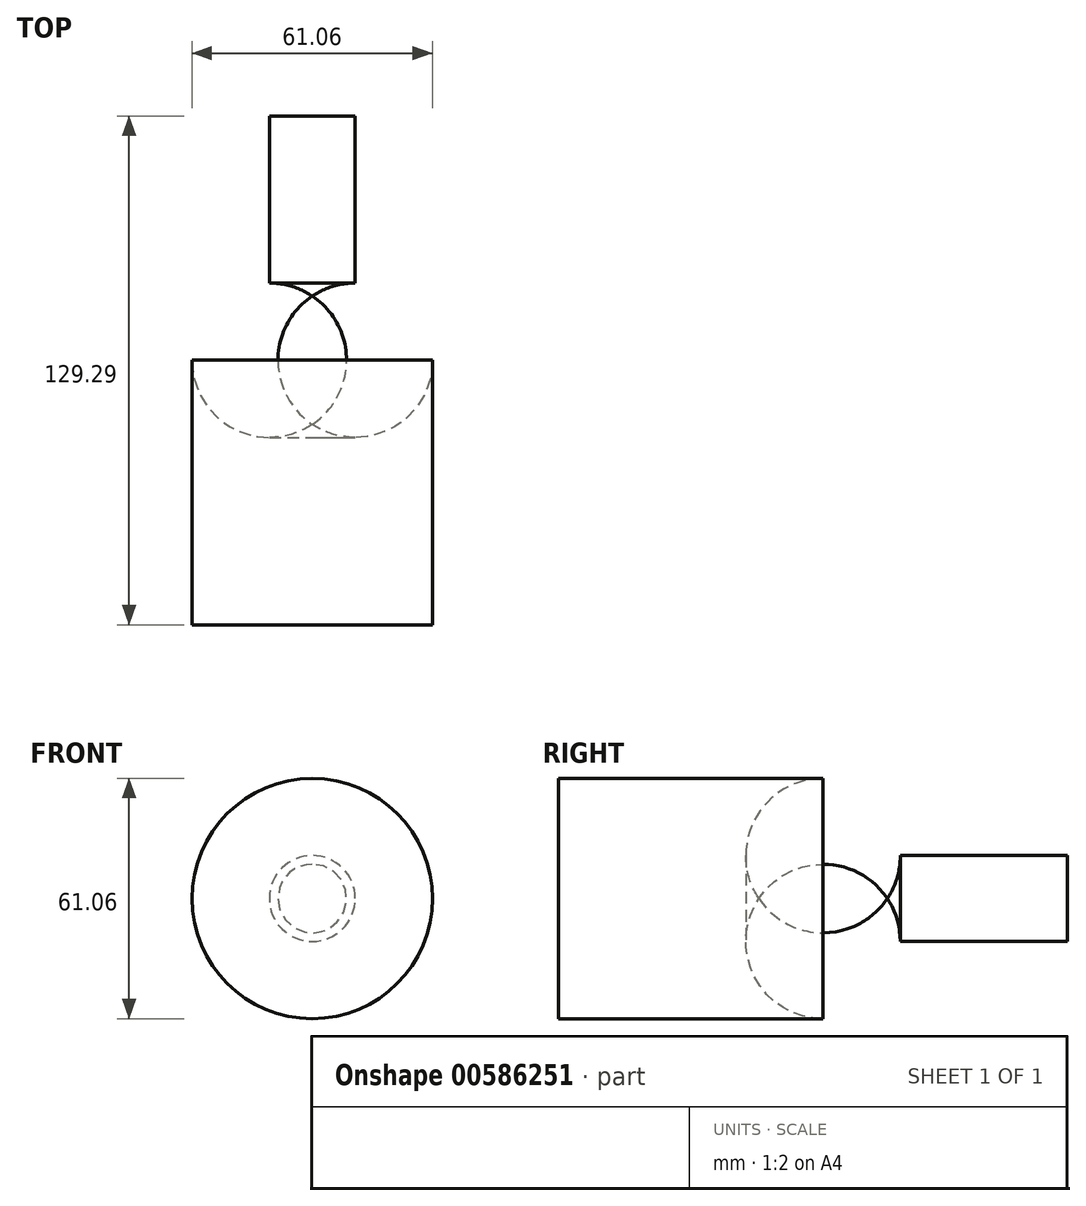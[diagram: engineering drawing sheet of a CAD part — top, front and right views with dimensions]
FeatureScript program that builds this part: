
annotation { "Feature Type Name" : "Feature", "Feature Type Description" : "" }
export const myFeature = defineFeature(function(context is Context, id is Id, definition is map)
    precondition{}
    {
        {
            var Q0;
            Q0=qCreatedBy(makeId("Front.planeOp"),FACE);
            var sketch = newSketch(context, id + "F0", { "sketchPlane" : qUnion([Q0])});
            skCircle(sketch, "E0", {"center": v(0, 0) * mm, "radius": 30.53 * mm});
            skSolve(sketch);
        }
        {
            var Q0;
            Q0=makeQuery(id+"F0.imprint","IMPRINT",FACE,{"disambiguationData":[TD([[makeQuery(id+"F0.imprint","IMPRINT",EDGE,{"derivedFrom":sQuery(id+"F0.wireOp",EDGE,"E0")}),1.0]])]});
            extrude(context, id + "F1", {"entities" : qUnion([Q0]), "oppositeDirection" : true, "depth" : 86.87 * mm, "offsetDistance" : 25.4 * mm});
        }
        {
            var Q0;
            Q0=makeQuery(id+"F1.opExtrude","CAP_EDGE",EDGE,{"disambiguationData":[OSD([sQuery(id+"F0.wireOp",EDGE,"E0")])],"isStart":false});
            fillet(context, id + "F2", {"entities" : qUnion([Q0]), "radius" : 19.62 * mm, "tangentPropagation" : true, "allowEdgeOverflow" : false});
        }
        {
            var Q0;
            Q0=makeQuery(id+"F1.opExtrude","CAP_FACE",FACE,{"disambiguationData":[OSD([sQuery(id+"F0.wireOp",EDGE,"E0")])],"isStart":false});
            extrude(context, id + "F3", {"entities" : qUnion([Q0]), "operationType" : NewBodyOperationType.ADD, "depth" : 42.42 * mm, "offsetDistance" : 25.4 * mm});
        }
    });
